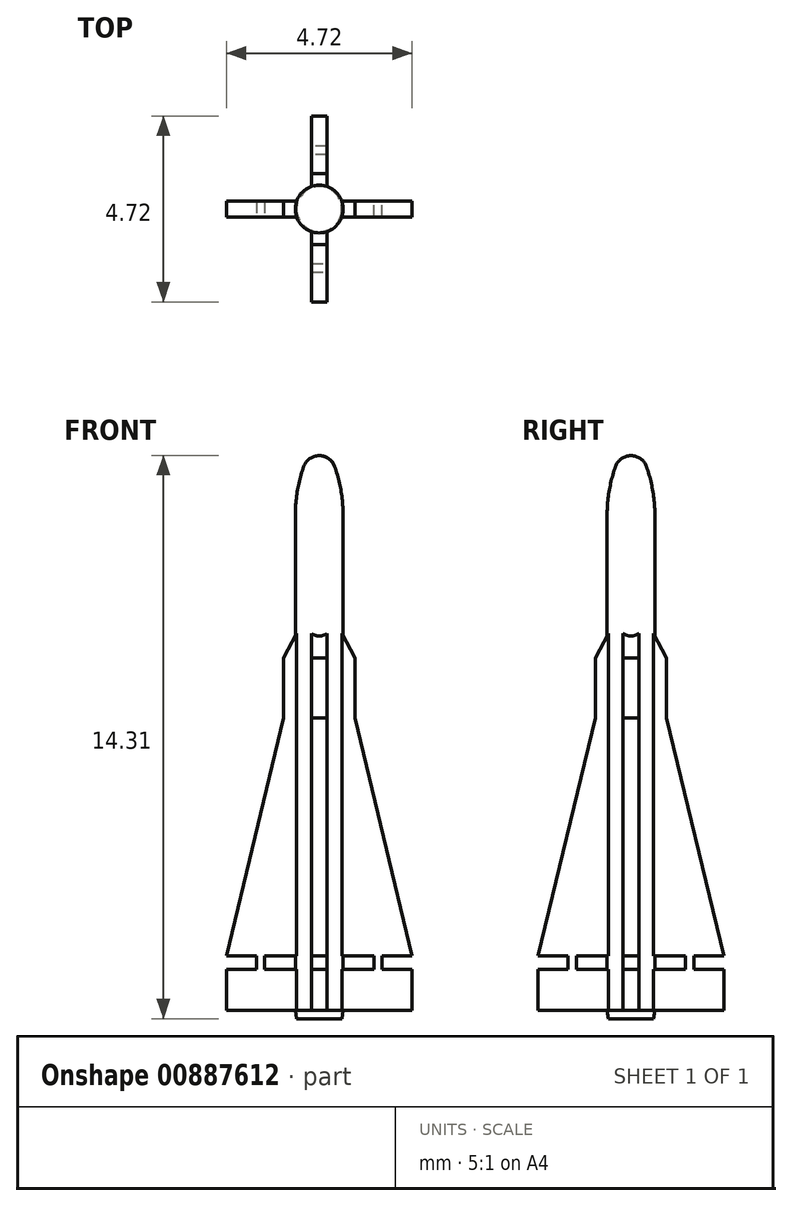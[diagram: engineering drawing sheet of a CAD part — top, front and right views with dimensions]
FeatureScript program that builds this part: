
annotation { "Feature Type Name" : "Feature", "Feature Type Description" : "" }
export const myFeature = defineFeature(function(context is Context, id is Id, definition is map)
    precondition{}
    {
        {
            var Q0;
            Q0=qCreatedBy(makeId("Front.planeOp"),FACE);
            var sketch = newSketch(context, id + "F0", { "sketchPlane" : qUnion([Q0])});
            skLineSegment(sketch, "E0", {"start": v(0, 0) * mm, "end": v(0, 14.3) * mm});
            skLineSegment(sketch, "E1", {"start": v(0.6, 12.78) * mm, "end": v(0.6, 0) * mm});
            skLineSegment(sketch, "E2", {"start": v(0.6, 0) * mm, "end": v(0, 0) * mm});
            skLineSegment(sketch, "E3", {"start": v(0.6, 0.2) * mm, "end": v(0.57, 0) * mm});
            skArc(sketch, "E4", {"start": v(0.4, 14.03) * mm, "mid": v(0.24, 14.23) * mm, "end": v(0, 14.3) * mm});
            skArc(sketch, "E5", {"start": v(0.6, 12.78) * mm, "mid": v(0.55, 13.41) * mm, "end": v(0.4, 14.03) * mm});
            skSolve(sketch);
        }
        {
            var Q0;
            {var subQ0=sQuery(id+"F0.wireOp",EDGE,"mrwio9nY-PsAZ-Zbfy-NhIU-sYq0QVbgGXAG");Q0=makeQuery(id+"F0.imprint","IMPRINT",FACE,{"disambiguationData":[TD([[makeQuery(id+"F0.imprint","IMPRINT",EDGE,{"derivedFrom":subQ0}),-1.0]])]});}
            var Q1;
            {var subQ7=sQuery(id+"F0.wireOp",EDGE,"E0");Q1=makeQuery(id+"F0.imprint","IMPRINT",FACE,{"disambiguationData":[TD([[makeQuery(id+"F0.imprint","IMPRINT",EDGE,{"derivedFrom":subQ7}),-1.0]])]});}
            var Q2;
            Q2=sQuery(id+"F0.wireOp",EDGE,"E0");
            revolve(context, id + "F1", {"surfaceOperationType" : NewSurfaceOperationType.NEW, "entities" : qUnion([Q0, Q1]), "axis" : qUnion([Q2]), "revolveType" : RevolveType.FULL});
        }
        {
            var Q0;
            Q0=qCreatedBy(makeId("Front.planeOp"),FACE);
            var sketch = newSketch(context, id + "F2", { "sketchPlane" : qUnion([Q0])});
            skLineSegment(sketch, "E6", {"start": v(0, 0) * mm, "end": v(0, 10.87) * mm});
            skLineSegment(sketch, "E7", {"start": v(0.4, 1.6) * mm, "end": v(0.4, 1.25) * mm});
            skLineSegment(sketch, "E8", {"start": v(0.4, 1.25) * mm, "end": v(2.36, 1.25) * mm});
            skLineSegment(sketch, "E9", {"start": v(0.6, 0) * mm, "end": v(0.6, 32.87) * mm, "construction": true});
            skLineSegment(sketch, "E10", {"start": v(0.4, 1.6) * mm, "end": v(2.36, 1.6) * mm});
            skLineSegment(sketch, "E11", {"start": v(2.36, 1.6) * mm, "end": v(0.9, 7.64) * mm});
            skPoint(sketch, "E12", {"position": v(0.6, 1.6) * mm});
            skLineSegment(sketch, "E13", {"start": v(0, 0.2) * mm, "end": v(2.36, 0.2) * mm});
            skLineSegment(sketch, "E14", {"start": v(2.36, 0.2) * mm, "end": v(2.36, 1.25) * mm});
            skLineSegment(sketch, "E15", {"start": v(1.39, 1.6) * mm, "end": v(1.39, 1.25) * mm});
            skLineSegment(sketch, "E16", {"start": v(1.6, 1.6) * mm, "end": v(1.6, 1.25) * mm});
            skLineSegment(sketch, "E17.0", {"start": v(0.6, 0.2) * mm, "end": v(-0.6, 0.2) * mm});
            skLineSegment(sketch, "E18", {"start": v(0.9, 7.64) * mm, "end": v(0.9, 9.17) * mm});
            skPoint(sketch, "E19", {"position": v(0.6, 9.72) * mm});
            skLineSegment(sketch, "E20", {"start": v(0.9, 9.17) * mm, "end": v(0, 10.87) * mm});
            skLineSegment(sketch, "E21.0", {"start": v(0.4, 14.03) * mm, "end": v(-0.4, 14.03) * mm});
            skSolve(sketch);
        }
        {
            var Q0;
            {var subQ3=sQuery(id+"F2.wireOp",EDGE,"E15");var subQ14=sQuery(id+"F2.wireOp",EDGE,"E7");Q0=qUnion([makeQuery(id+"F2.imprint","IMPRINT",FACE,{"disambiguationData":[TD([[makeQuery(id+"F2.imprint","IMPRINT",EDGE,{"derivedFrom":subQ14}),-1.0]])]}),makeQuery(id+"F2.imprint","IMPRINT",FACE,{"disambiguationData":[TD([[makeQuery(id+"F2.imprint","IMPRINT",EDGE,{"derivedFrom":subQ3}),1.0]])]})]);}
            extrude(context, id + "F3", {"entities" : qUnion([Q0]), "operationType" : NewBodyOperationType.ADD, "depth" : .4 * mm, "offsetDistance" : 25 * mm, "symmetric" : true});
        }
        {
            var Q0;
            Q0=makeQuery(id+"F1.opRevolve","SWEPT_BODY",BODY,{"disambiguationData":[OSD([sQuery(id+"F0.wireOp",EDGE,"E0"),sQuery(id+"F0.wireOp",EDGE,"E1"),sQuery(id+"F0.wireOp",EDGE,"E2"),sQuery(id+"F0.wireOp",EDGE,"2EiOItwe-9FNA-eY8p-DkXH-AMy5AHyUmzZA"),sQuery(id+"F0.wireOp",EDGE,"lF35QjYl-MEgV-fRWE-0Yr6-Bt5vS8A7brRf")])]});
            var Q1;
            Q1=makeQuery(id+"F1.opRevolve","SWEPT_FACE",FACE,{"disambiguationData":[OSD([sQuery(id+"F0.wireOp",EDGE,"E1")])]});
            circularPattern(context, id + "F4", {"operationType" : NewBodyOperationType.ADD, "entities" : qUnion([Q0]), "axis" : qUnion([Q1]), "angle" : 360 * degree, "instanceCount" : 4, "equalSpace" : true, "computeTransformsWithoutBuiltin" : true});
        }
    });
